# Revit family: ShowerHead-Vitra-LiteSeries-A45646
name_source: partatom
category: Plumbing Fixtures
revit_build: Autodesk Revit 2017 (Build: 20160225_1515(x64)
units: mm (PartAtom-declared; Revit-internal decimal feet)

## family parameters
Always vertical = No
Cut with Voids When Loaded = No
OmniClass Number = 23.45.00.00
OmniClass Title = Sanitary, Laundry, and Cleaning Equipment
Part Type = Normal
Room Calculation Point = No
Round Connector Dimension = Use Diameter
Shared = Yes
Work Plane-Based = Yes

## types (4) — shared parameters
BIMobject category = Showers
CW Connection = Yes
Connection Diameter (mm) = 15 mm  [stored 0.0492126 ft]
Default Elevation = 2300 mm
Description = Lite LC Duş Başlığı
Design country = Turkey
HW Connection = Yes
IFC Classification = Sanitary Terminal
Manufacturer = Vitra
Manufacturer name = Vitra
Masterformat 2014 Code = 22 41 23
Masterformat 2014 Description = Residential Showers
Nominal Depth (mm) = 400 mm  [stored 1.31234 ft]
Nominal Height (mm) = 65 mm  [stored 0.213255 ft]
Nominal Width (mm) = 400 mm  [stored 1.31234 ft]
Number Of Connections = 1
OmniClass Code = 23-31 17 19
OmniClass Description = Shower Head Fixtures
Product Properties = Shower Head  18 L/min.
Product Type = Lite LC Shower Head
Product certification = https://www.vitraglobal.com
Product family = Lite Series
Product group = Shower Heads
URL = https://vitraglobal.com
Uniclass 1.4 Code = L7214
Uniclass 1.4 Description = Showers
Uniclass 2.0 Code = PR-35-06-81
Uniclass 2.0 Description = Shower Heads
Uniclass 2015 Code = Pr_40_20_87_76
Uniclass 2015 Name = Shower heads
Uniformat II Code = D2010
Uniformat II Description = Plumbing Fixtures
Vent Connection = No
Warranty Period (Year) = 5
Waste Connection = No
Weight Net (kg) = 2.2

## per-type parameters (varying)
| type | Article No. (default) | Brand | Coating Material | Color | Model | Product SKU | Product url | Technical description |
| ShowerHead-Vitra-LiteSeries-A45646 | A45646 | Artema | Chrome | Chrome | A45646 | A45646 | https://www.vitra.com.tr | https://www.vitra.com.tr |
| ShowerHead-Vitra-LiteSeries-A4564623 | A4564623 | Artema | Gold | Gold | A4564623 | A4564623 | https://www.vitra.com.tr | https://www.vitra.com.tr |
| ShowerHead-Vitra-LiteSeries-A45646EXP | A45646EXP | VitrA | Chrome | Chrome | A45646EXP | A45646EXP | https://www.vitraglobal.com | https://www.vitraglobal.com |
| ShowerHead-Vitra-LiteSeries-A4564623EXP | A4564623EXP | VitrA | Gold | Gold | A4564623EXP | A4564623EXP | https://www.vitra-india.com | https://www.vitra-india.com |

note: [stored X ft] marks values corroborated as IEEE doubles in the binary element streams (Revit-internal decimal feet)

## geometry (parser evidence)
native form markers: Sweep x3
no freeform markers — native parametric forms only
